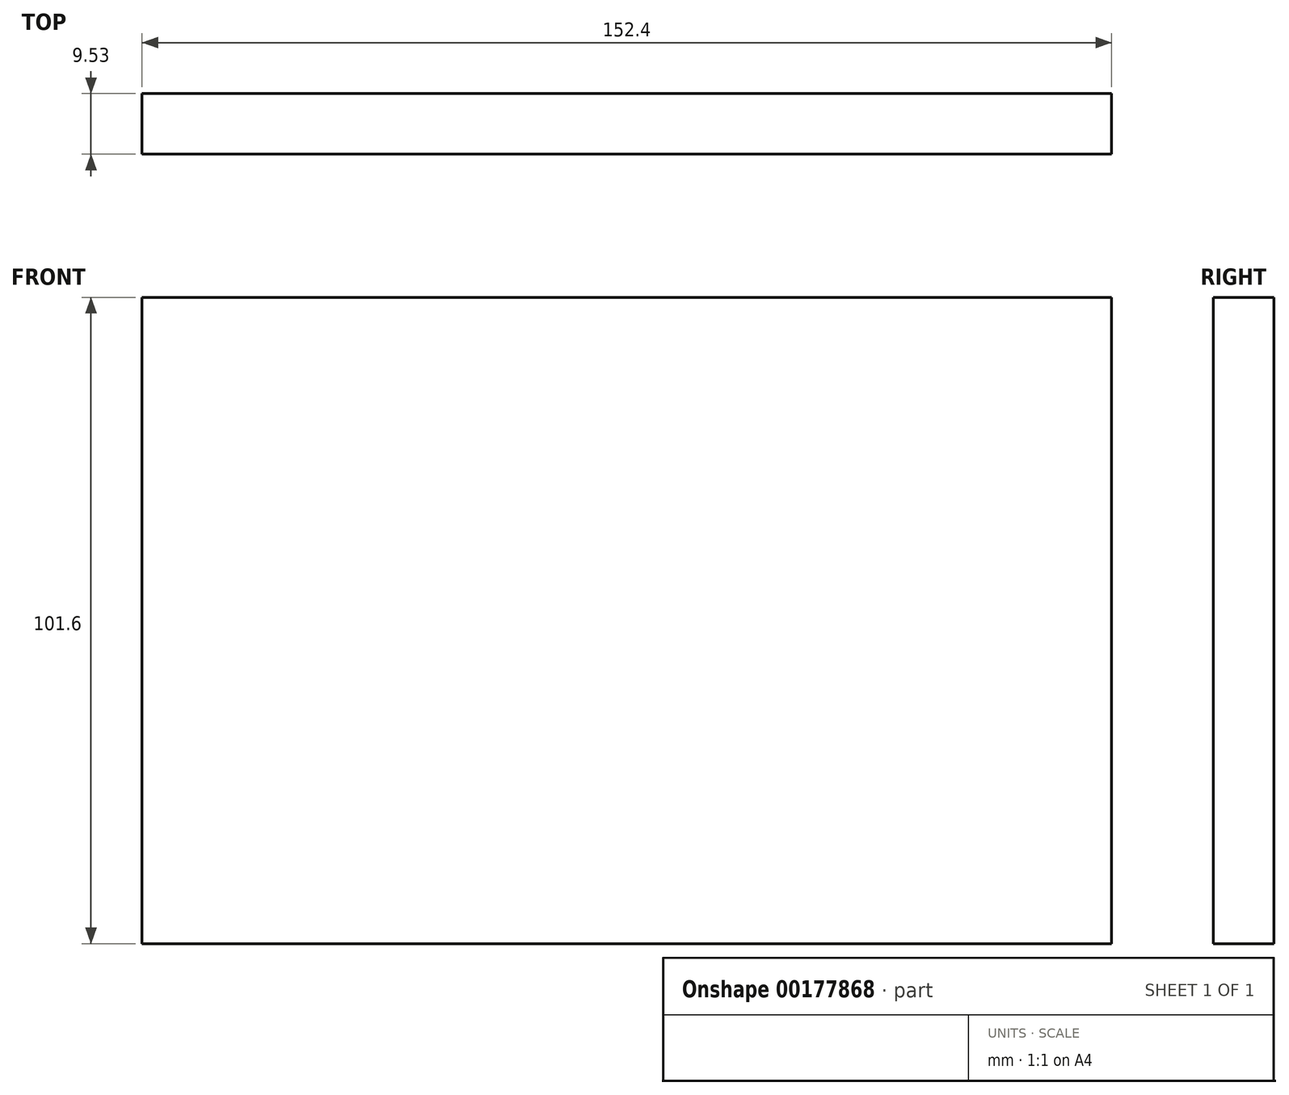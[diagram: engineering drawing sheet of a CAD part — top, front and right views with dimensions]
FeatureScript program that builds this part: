
annotation { "Feature Type Name" : "Feature", "Feature Type Description" : "" }
export const myFeature = defineFeature(function(context is Context, id is Id, definition is map)
    precondition{}
    {
        {
            var Q0;
            Q0=qCreatedBy(makeId("Front.planeOp"),FACE);
            var sketch = newSketch(context, id + "F0", { "sketchPlane" : qUnion([Q0])});
            skLineSegment(sketch, "E0.bottom", {"start": v(-25.4, 77.22) * mm, "end": v(127, 77.22) * mm});
            skLineSegment(sketch, "E0.top", {"start": v(-25.4, -24.38) * mm, "end": v(127, -24.38) * mm});
            skLineSegment(sketch, "E0.left", {"start": v(-25.4, 77.22) * mm, "end": v(-25.4, -24.38) * mm});
            skLineSegment(sketch, "E0.right", {"start": v(127, 77.22) * mm, "end": v(127, -24.38) * mm});
            skSolve(sketch);
        }
        {
            var Q0;
            Q0 = qSketchRegion(id + "F0", true);
            extrude(context, id + "F1", {"entities" : qUnion([Q0]), "depth" : 9.52 * mm});
        }
    });
